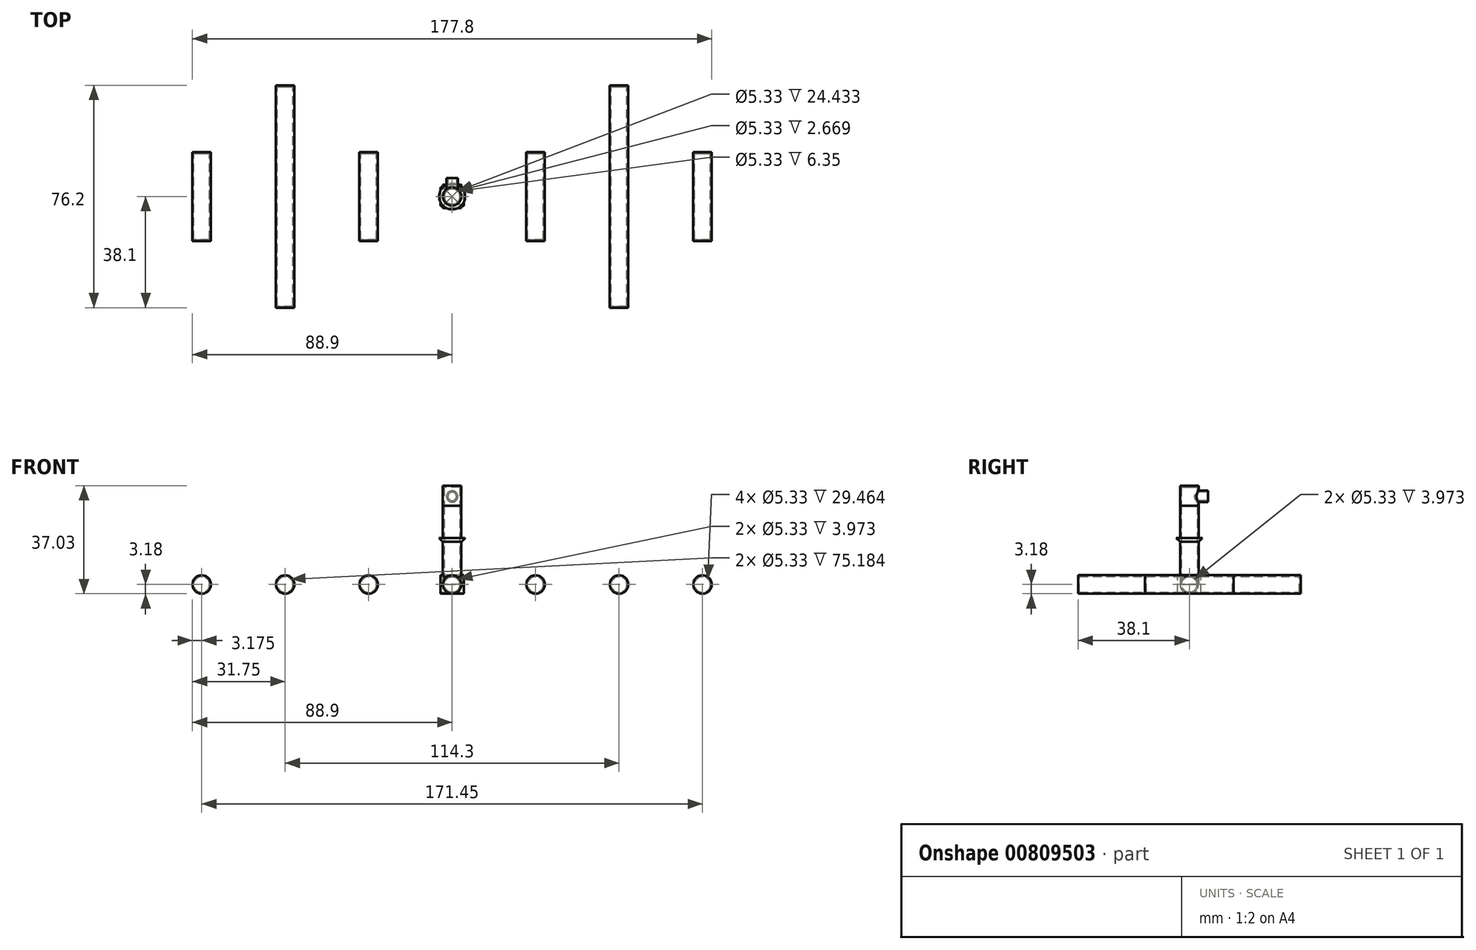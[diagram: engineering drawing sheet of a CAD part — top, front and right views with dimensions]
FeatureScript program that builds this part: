
annotation { "Feature Type Name" : "Feature", "Feature Type Description" : "" }
export const myFeature = defineFeature(function(context is Context, id is Id, definition is map)
    precondition{}
    {
        {
            var Q0;
            Q0=qCreatedBy(makeId("Front.planeOp"),FACE);
            var sketch = newSketch(context, id + "F0", { "sketchPlane" : qUnion([Q0])});
            skCircle(sketch, "E0", {"center": v(0, 0) * mm, "radius": 3.18 * mm});
            skCircle(sketch, "E1", {"center": v(0, 0) * mm, "radius": 2.67 * mm});
            skSolve(sketch);
        }
        {
            var Q0;
            Q0 = qSketchRegion(id + "F0", true);
            extrude(context, id + "F1", {"entities" : qUnion([Q0]), "depth" : (3 * sqrt(2) - 0.25) * mm, "offsetDistance" : 25.4 * mm, "hasSecondDirection" : true, "secondDirectionOppositeDirection" : true, "secondDirectionDepth" : (3 * sqrt(2) - 0.25) * mm});
        }
        {
            var Q0;
            Q0=makeQuery(id+"F0.imprint","IMPRINT",FACE,{"disambiguationData":[TD([[makeQuery(id+"F0.imprint","IMPRINT",EDGE,{"derivedFrom":sQuery(id+"F0.wireOp",EDGE,"E1")}),1.0]])]});
            var Q1;
            Q1=makeQuery(id+"F0.imprint","IMPRINT",FACE,{"disambiguationData":[TD([[makeQuery(id+"F0.imprint","IMPRINT",EDGE,{"derivedFrom":sQuery(id+"F0.wireOp",EDGE,"E0")}),1.0]])]});
            extrude(context, id + "F2", {"entities" : qUnion([Q0, Q1]), "operationType" : NewBodyOperationType.ADD, "depth" : (3 * sqrt(2) - 0.25) * mm, "offsetDistance" : 25.4 * mm, "hasSecondDirection" : true, "secondDirectionOppositeDirection" : false, "secondDirectionDepth" : ((3 * sqrt(2) - 0.25) - 0.02) * mm});
        }
        {
            var Q0;
            Q0=makeQuery(id+"F0.imprint","IMPRINT",FACE,{"disambiguationData":[TD([[makeQuery(id+"F0.imprint","IMPRINT",EDGE,{"derivedFrom":sQuery(id+"F0.wireOp",EDGE,"E1")}),1.0]])]});
            var Q1;
            Q1=makeQuery(id+"F0.imprint","IMPRINT",FACE,{"disambiguationData":[TD([[makeQuery(id+"F0.imprint","IMPRINT",EDGE,{"derivedFrom":sQuery(id+"F0.wireOp",EDGE,"E0")}),1.0]])]});
            extrude(context, id + "F3", {"entities" : qUnion([Q0, Q1]), "operationType" : NewBodyOperationType.ADD, "oppositeDirection" : true, "depth" : (3 * sqrt(2) - 0.25) * mm, "offsetDistance" : 25.4 * mm, "hasSecondDirection" : true, "secondDirectionOppositeDirection" : true, "secondDirectionDepth" : ((3 * sqrt(2) - 0.25) - 0.02) * mm});
        }
        {
            var Q0;
            Q0=qCreatedBy(makeId("Right.planeOp"),FACE);
            var sketch = newSketch(context, id + "F4", { "sketchPlane" : qUnion([Q0])});
            skLineSegment(sketch, "E2", {"start": v(0, 0) * mm, "end": v(0, 50.22) * mm});
            skSolve(sketch);
        }
        {
            var Q0;
            Q0=makeQuery(id+"F1.opExtrude","SWEPT_BODY",BODY,{"disambiguationData":[OSD([sQuery(id+"F0.wireOp",EDGE,"E0"),sQuery(id+"F0.wireOp",EDGE,"E1")])]});
            var Q1;
            Q1=sQuery(id+"F4.wireOp",EDGE,"E2");
            circularPattern(context, id + "F5", {"entities" : qUnion([Q0]), "axis" : qUnion([Q1]), "angle" : 360 * degree, "instanceCount" : 4, "equalSpace" : true});
        }
        {
            var Q0;
            Q0=makeQuery(id+"F5.opPattern","COPY",BODY,{"derivedFrom":makeQuery(id+"F1.opExtrude","SWEPT_BODY",BODY,{"disambiguationData":[OSD([sQuery(id+"F0.wireOp",EDGE,"E0"),sQuery(id+"F0.wireOp",EDGE,"E1")])]}),"instanceName":"3"});
            deleteBodies(context, id + "F6", {"entities" : qUnion([Q0])});
        }
        {
            var Q0;
            Q0=makeQuery(id+"F5.opPattern","COPY",BODY,{"derivedFrom":makeQuery(id+"F1.opExtrude","SWEPT_BODY",BODY,{"disambiguationData":[OSD([sQuery(id+"F0.wireOp",EDGE,"E0"),sQuery(id+"F0.wireOp",EDGE,"E1")])]}),"instanceName":"2"});
            deleteBodies(context, id + "F7", {"entities" : qUnion([Q0])});
        }
        {
            var Q0;
            Q0=qCreatedBy(makeId("Top.planeOp"),FACE);
            var sketch = newSketch(context, id + "F8", { "sketchPlane" : qUnion([Q0])});
            skLineSegment(sketch, "E3", {"start": v(0, 0) * mm, "end": v(0, 107.76) * mm, "construction": true});
            skLineSegment(sketch, "E4", {"start": v(0, 107.76) * mm, "end": v(107.76, 0) * mm});
            skLineSegment(sketch, "E5", {"start": v(107.76, 0) * mm, "end": v(0, -107.76) * mm});
            skLineSegment(sketch, "E6", {"start": v(0, -107.76) * mm, "end": v(-107.76, 0) * mm});
            skLineSegment(sketch, "E7", {"start": v(-107.76, 0) * mm, "end": v(0, 107.76) * mm});
            skSolve(sketch);
        }
        {
            var Q0;
            Q0=qCreatedBy(makeId("Front.planeOp"),FACE);
            var sketch = newSketch(context, id + "F9", { "sketchPlane" : qUnion([Q0])});
            skLineSegment(sketch, "E8", {"start": v(0, 0) * mm, "end": v(28.58, 0) * mm, "construction": true});
            skLineSegment(sketch, "E9", {"start": v(28.58, 0) * mm, "end": v(57.15, 0) * mm, "construction": true});
            skLineSegment(sketch, "E10", {"start": v(57.15, 0) * mm, "end": v(85.73, 0) * mm, "construction": true});
            skLineSegment(sketch, "E11", {"start": v(0, 0) * mm, "end": v(-28.58, 0) * mm, "construction": true});
            skLineSegment(sketch, "E12", {"start": v(-28.58, 0) * mm, "end": v(-57.15, 0) * mm, "construction": true});
            skLineSegment(sketch, "E13", {"start": v(-57.15, 0) * mm, "end": v(-85.73, 0) * mm, "construction": true});
            skLineSegment(sketch, "E14", {"start": v(0, 0) * mm, "end": v(-101.41, 0) * mm, "construction": true});
            skLineSegment(sketch, "E15", {"start": v(0, 0) * mm, "end": v(101.41, 0) * mm, "construction": true});
            skCircle(sketch, "E16", {"center": v(-85.73, 0) * mm, "radius": 3.18 * mm});
            skCircle(sketch, "E17", {"center": v(-57.15, 0) * mm, "radius": 3.18 * mm});
            skCircle(sketch, "E18", {"center": v(-28.58, 0) * mm, "radius": 3.18 * mm});
            skCircle(sketch, "E19", {"center": v(28.58, 0) * mm, "radius": 3.18 * mm});
            skCircle(sketch, "E20", {"center": v(57.15, 0) * mm, "radius": 3.18 * mm});
            skCircle(sketch, "E21", {"center": v(85.73, 0) * mm, "radius": 3.18 * mm});
            skCircle(sketch, "E22", {"center": v(-85.73, 0) * mm, "radius": 2.67 * mm});
            skCircle(sketch, "E23", {"center": v(-57.15, 0) * mm, "radius": 2.67 * mm});
            skCircle(sketch, "E24", {"center": v(-28.58, 0) * mm, "radius": 2.67 * mm});
            skCircle(sketch, "E25", {"center": v(28.58, 0) * mm, "radius": 2.67 * mm});
            skCircle(sketch, "E26", {"center": v(57.15, 0) * mm, "radius": 2.67 * mm});
            skCircle(sketch, "E27", {"center": v(85.73, 0) * mm, "radius": 2.67 * mm});
            skSolve(sketch);
        }
        {
            var Q0;
            Q0=makeQuery(id+"F9.imprint","IMPRINT",FACE,{"disambiguationData":[TD([[makeQuery(id+"F9.imprint","IMPRINT",EDGE,{"derivedFrom":sQuery(id+"F9.wireOp",EDGE,"E22")}),1.0]])]});
            var Q1;
            Q1=makeQuery(id+"F9.imprint","IMPRINT",FACE,{"disambiguationData":[TD([[makeQuery(id+"F9.imprint","IMPRINT",EDGE,{"derivedFrom":sQuery(id+"F9.wireOp",EDGE,"E23")}),1.0]])]});
            var Q2;
            Q2=makeQuery(id+"F9.imprint","IMPRINT",FACE,{"disambiguationData":[TD([[makeQuery(id+"F9.imprint","IMPRINT",EDGE,{"derivedFrom":sQuery(id+"F9.wireOp",EDGE,"E24")}),1.0]])]});
            var Q3;
            Q3=makeQuery(id+"F9.imprint","IMPRINT",FACE,{"disambiguationData":[TD([[makeQuery(id+"F9.imprint","IMPRINT",EDGE,{"derivedFrom":sQuery(id+"F9.wireOp",EDGE,"E25")}),1.0]])]});
            var Q4;
            Q4=makeQuery(id+"F9.imprint","IMPRINT",FACE,{"disambiguationData":[TD([[makeQuery(id+"F9.imprint","IMPRINT",EDGE,{"derivedFrom":sQuery(id+"F9.wireOp",EDGE,"E26")}),1.0]])]});
            var Q5;
            Q5=makeQuery(id+"F9.imprint","IMPRINT",FACE,{"disambiguationData":[TD([[makeQuery(id+"F9.imprint","IMPRINT",EDGE,{"derivedFrom":sQuery(id+"F9.wireOp",EDGE,"E27")}),1.0]])]});
            extrude(context, id + "F10", {"entities" : qUnion([Q0, Q1, Q2, Q3, Q4, Q5]), "operationType" : NewBodyOperationType.REMOVE, "oppositeDirection" : true, "depth" : 25.4 * mm, "offsetDistance" : 25.4 * mm, "hasSecondDirection" : true, "secondDirectionOppositeDirection" : false, "secondDirectionDepth" : 25.4 * mm});
        }
        {
            var Q0;
            Q0=makeQuery(id+"F9.imprint","IMPRINT",FACE,{"disambiguationData":[TD([[makeQuery(id+"F9.imprint","IMPRINT",EDGE,{"derivedFrom":sQuery(id+"F9.wireOp",EDGE,"E16")}),1.0]])]});
            var Q1;
            Q1=makeQuery(id+"F9.imprint","IMPRINT",FACE,{"disambiguationData":[TD([[makeQuery(id+"F9.imprint","IMPRINT",EDGE,{"derivedFrom":sQuery(id+"F9.wireOp",EDGE,"E18")}),1.0]])]});
            var Q2;
            Q2=makeQuery(id+"F9.imprint","IMPRINT",FACE,{"disambiguationData":[TD([[makeQuery(id+"F9.imprint","IMPRINT",EDGE,{"derivedFrom":sQuery(id+"F9.wireOp",EDGE,"E19")}),1.0]])]});
            var Q3;
            Q3=makeQuery(id+"F9.imprint","IMPRINT",FACE,{"disambiguationData":[TD([[makeQuery(id+"F9.imprint","IMPRINT",EDGE,{"derivedFrom":sQuery(id+"F9.wireOp",EDGE,"E21")}),1.0]])]});
            extrude(context, id + "F11", {"entities" : qUnion([Q0, Q1, Q2, Q3]), "operationType" : NewBodyOperationType.ADD, "depth" : 15.24 * mm, "offsetDistance" : 25.4 * mm, "hasSecondDirection" : true, "secondDirectionOppositeDirection" : true, "secondDirectionDepth" : 15.24 * mm});
        }
        {
            var Q0;
            Q0=makeQuery(id+"F9.imprint","IMPRINT",FACE,{"disambiguationData":[TD([[makeQuery(id+"F9.imprint","IMPRINT",EDGE,{"derivedFrom":sQuery(id+"F9.wireOp",EDGE,"E22")}),1.0]])]});
            var Q1;
            Q1=makeQuery(id+"F9.imprint","IMPRINT",FACE,{"disambiguationData":[TD([[makeQuery(id+"F9.imprint","IMPRINT",EDGE,{"derivedFrom":sQuery(id+"F9.wireOp",EDGE,"E16")}),1.0]])]});
            var Q2;
            Q2=makeQuery(id+"F9.imprint","IMPRINT",FACE,{"disambiguationData":[TD([[makeQuery(id+"F9.imprint","IMPRINT",EDGE,{"derivedFrom":sQuery(id+"F9.wireOp",EDGE,"E24")}),1.0]])]});
            var Q3;
            Q3=makeQuery(id+"F9.imprint","IMPRINT",FACE,{"disambiguationData":[TD([[makeQuery(id+"F9.imprint","IMPRINT",EDGE,{"derivedFrom":sQuery(id+"F9.wireOp",EDGE,"E18")}),1.0]])]});
            var Q4;
            Q4=makeQuery(id+"F9.imprint","IMPRINT",FACE,{"disambiguationData":[TD([[makeQuery(id+"F9.imprint","IMPRINT",EDGE,{"derivedFrom":sQuery(id+"F9.wireOp",EDGE,"E25")}),1.0]])]});
            var Q5;
            Q5=makeQuery(id+"F9.imprint","IMPRINT",FACE,{"disambiguationData":[TD([[makeQuery(id+"F9.imprint","IMPRINT",EDGE,{"derivedFrom":sQuery(id+"F9.wireOp",EDGE,"E19")}),1.0]])]});
            var Q6;
            Q6=makeQuery(id+"F9.imprint","IMPRINT",FACE,{"disambiguationData":[TD([[makeQuery(id+"F9.imprint","IMPRINT",EDGE,{"derivedFrom":sQuery(id+"F9.wireOp",EDGE,"E27")}),1.0]])]});
            var Q7;
            Q7=makeQuery(id+"F9.imprint","IMPRINT",FACE,{"disambiguationData":[TD([[makeQuery(id+"F9.imprint","IMPRINT",EDGE,{"derivedFrom":sQuery(id+"F9.wireOp",EDGE,"E21")}),1.0]])]});
            extrude(context, id + "F12", {"entities" : qUnion([Q0, Q1, Q2, Q3, Q4, Q5, Q6, Q7]), "operationType" : NewBodyOperationType.ADD, "depth" : 15.24 * mm, "offsetDistance" : 25.4 * mm, "hasSecondDirection" : true, "secondDirectionOppositeDirection" : false, "secondDirectionDepth" : 14.73 * mm});
        }
        {
            var Q0;
            Q0=makeQuery(id+"F9.imprint","IMPRINT",FACE,{"disambiguationData":[TD([[makeQuery(id+"F9.imprint","IMPRINT",EDGE,{"derivedFrom":sQuery(id+"F9.wireOp",EDGE,"E22")}),1.0]])]});
            var Q1;
            Q1=makeQuery(id+"F9.imprint","IMPRINT",FACE,{"disambiguationData":[TD([[makeQuery(id+"F9.imprint","IMPRINT",EDGE,{"derivedFrom":sQuery(id+"F9.wireOp",EDGE,"E16")}),1.0]])]});
            var Q2;
            Q2=makeQuery(id+"F9.imprint","IMPRINT",FACE,{"disambiguationData":[TD([[makeQuery(id+"F9.imprint","IMPRINT",EDGE,{"derivedFrom":sQuery(id+"F9.wireOp",EDGE,"E24")}),1.0]])]});
            var Q3;
            Q3=makeQuery(id+"F9.imprint","IMPRINT",FACE,{"disambiguationData":[TD([[makeQuery(id+"F9.imprint","IMPRINT",EDGE,{"derivedFrom":sQuery(id+"F9.wireOp",EDGE,"E18")}),1.0]])]});
            var Q4;
            Q4=makeQuery(id+"F9.imprint","IMPRINT",FACE,{"disambiguationData":[TD([[makeQuery(id+"F9.imprint","IMPRINT",EDGE,{"derivedFrom":sQuery(id+"F9.wireOp",EDGE,"E25")}),1.0]])]});
            var Q5;
            Q5=makeQuery(id+"F9.imprint","IMPRINT",FACE,{"disambiguationData":[TD([[makeQuery(id+"F9.imprint","IMPRINT",EDGE,{"derivedFrom":sQuery(id+"F9.wireOp",EDGE,"E19")}),1.0]])]});
            var Q6;
            Q6=makeQuery(id+"F9.imprint","IMPRINT",FACE,{"disambiguationData":[TD([[makeQuery(id+"F9.imprint","IMPRINT",EDGE,{"derivedFrom":sQuery(id+"F9.wireOp",EDGE,"E27")}),1.0]])]});
            var Q7;
            Q7=makeQuery(id+"F9.imprint","IMPRINT",FACE,{"disambiguationData":[TD([[makeQuery(id+"F9.imprint","IMPRINT",EDGE,{"derivedFrom":sQuery(id+"F9.wireOp",EDGE,"E21")}),1.0]])]});
            extrude(context, id + "F13", {"entities" : qUnion([Q0, Q1, Q2, Q3, Q4, Q5, Q6, Q7]), "operationType" : NewBodyOperationType.ADD, "oppositeDirection" : true, "depth" : 15.24 * mm, "offsetDistance" : 25.4 * mm, "hasSecondDirection" : true, "secondDirectionOppositeDirection" : true, "secondDirectionDepth" : 14.73 * mm});
        }
        {
            var Q0;
            Q0=makeQuery(id+"F9.imprint","IMPRINT",FACE,{"disambiguationData":[TD([[makeQuery(id+"F9.imprint","IMPRINT",EDGE,{"derivedFrom":sQuery(id+"F9.wireOp",EDGE,"E17")}),1.0]])]});
            var Q1;
            Q1=makeQuery(id+"F9.imprint","IMPRINT",FACE,{"disambiguationData":[TD([[makeQuery(id+"F9.imprint","IMPRINT",EDGE,{"derivedFrom":sQuery(id+"F9.wireOp",EDGE,"E20")}),1.0]])]});
            extrude(context, id + "F14", {"entities" : qUnion([Q0, Q1]), "operationType" : NewBodyOperationType.ADD, "depth" : 38.1 * mm, "offsetDistance" : 25.4 * mm, "hasSecondDirection" : true, "secondDirectionOppositeDirection" : true, "secondDirectionDepth" : 38.1 * mm});
        }
        {
            var Q0;
            Q0=makeQuery(id+"F9.imprint","IMPRINT",FACE,{"disambiguationData":[TD([[makeQuery(id+"F9.imprint","IMPRINT",EDGE,{"derivedFrom":sQuery(id+"F9.wireOp",EDGE,"E26")}),1.0]])]});
            var Q1;
            Q1=makeQuery(id+"F9.imprint","IMPRINT",FACE,{"disambiguationData":[TD([[makeQuery(id+"F9.imprint","IMPRINT",EDGE,{"derivedFrom":sQuery(id+"F9.wireOp",EDGE,"E20")}),1.0]])]});
            var Q2;
            Q2=makeQuery(id+"F9.imprint","IMPRINT",FACE,{"disambiguationData":[TD([[makeQuery(id+"F9.imprint","IMPRINT",EDGE,{"derivedFrom":sQuery(id+"F9.wireOp",EDGE,"E23")}),1.0]])]});
            var Q3;
            Q3=makeQuery(id+"F9.imprint","IMPRINT",FACE,{"disambiguationData":[TD([[makeQuery(id+"F9.imprint","IMPRINT",EDGE,{"derivedFrom":sQuery(id+"F9.wireOp",EDGE,"E17")}),1.0]])]});
            extrude(context, id + "F15", {"entities" : qUnion([Q0, Q1, Q2, Q3]), "operationType" : NewBodyOperationType.ADD, "depth" : 38.1 * mm, "offsetDistance" : 25.4 * mm, "hasSecondDirection" : true, "secondDirectionOppositeDirection" : false, "secondDirectionDepth" : 37.6 * mm});
        }
        {
            var Q0;
            Q0=makeQuery(id+"F9.imprint","IMPRINT",FACE,{"disambiguationData":[TD([[makeQuery(id+"F9.imprint","IMPRINT",EDGE,{"derivedFrom":sQuery(id+"F9.wireOp",EDGE,"E23")}),1.0]])]});
            var Q1;
            Q1=makeQuery(id+"F9.imprint","IMPRINT",FACE,{"disambiguationData":[TD([[makeQuery(id+"F9.imprint","IMPRINT",EDGE,{"derivedFrom":sQuery(id+"F9.wireOp",EDGE,"E17")}),1.0]])]});
            var Q2;
            Q2=makeQuery(id+"F9.imprint","IMPRINT",FACE,{"disambiguationData":[TD([[makeQuery(id+"F9.imprint","IMPRINT",EDGE,{"derivedFrom":sQuery(id+"F9.wireOp",EDGE,"E26")}),1.0]])]});
            var Q3;
            Q3=makeQuery(id+"F9.imprint","IMPRINT",FACE,{"disambiguationData":[TD([[makeQuery(id+"F9.imprint","IMPRINT",EDGE,{"derivedFrom":sQuery(id+"F9.wireOp",EDGE,"E20")}),1.0]])]});
            extrude(context, id + "F16", {"entities" : qUnion([Q0, Q1, Q2, Q3]), "operationType" : NewBodyOperationType.ADD, "oppositeDirection" : true, "depth" : 38.1 * mm, "offsetDistance" : 25.4 * mm, "hasSecondDirection" : true, "secondDirectionOppositeDirection" : true, "secondDirectionDepth" : 37.6 * mm});
        }
        {
            var Q0;
            Q0=qCreatedBy(makeId("Right.planeOp"),FACE);
            var sketch = newSketch(context, id + "F17", { "sketchPlane" : qUnion([Q0])});
            skCircle(sketch, "E28", {"center": v(0, 0) * mm, "radius": 3.18 * mm});
            skCircle(sketch, "E29", {"center": v(0, 0) * mm, "radius": 2.67 * mm});
            skSolve(sketch);
        }
        {
            var Q0;
            Q0=makeQuery(id+"F17.imprint","IMPRINT",FACE,{"disambiguationData":[TD([[makeQuery(id+"F17.imprint","IMPRINT",EDGE,{"derivedFrom":sQuery(id+"F17.wireOp",EDGE,"E29")}),1.0]])]});
            extrude(context, id + "F18", {"entities" : qUnion([Q0]), "operationType" : NewBodyOperationType.REMOVE, "oppositeDirection" : true, "depth" : (3 * sqrt(2) - 0.25 - 0.02) * mm, "offsetDistance" : 25.4 * mm, "hasSecondDirection" : true, "secondDirectionOppositeDirection" : false, "secondDirectionDepth" : (3 * sqrt(2) - 0.25 - 0.02) * mm});
        }
        {
            var Q0;
            Q0=makeQuery(id+"F1.opExtrude","SWEPT_BODY",BODY,{"disambiguationData":[OSD([sQuery(id+"F0.wireOp",EDGE,"E0"),sQuery(id+"F0.wireOp",EDGE,"E1")])]});
            var Q1;
            Q1=sQuery(id+"F4.wireOp",EDGE,"E2");
            circularPattern(context, id + "F19", {"entities" : qUnion([Q0]), "axis" : qUnion([Q1]), "angle" : 360 * degree, "instanceCount" : 4, "equalSpace" : true});
        }
        {
            var Q0;
            Q0=makeQuery(id+"F19.opPattern","COPY",BODY,{"derivedFrom":makeQuery(id+"F1.opExtrude","SWEPT_BODY",BODY,{"disambiguationData":[OSD([sQuery(id+"F0.wireOp",EDGE,"E0"),sQuery(id+"F0.wireOp",EDGE,"E1")])]}),"instanceName":"3"});
            deleteBodies(context, id + "F20", {"entities" : qUnion([Q0])});
        }
        {
            var Q0;
            Q0=makeQuery(id+"F19.opPattern","COPY",BODY,{"derivedFrom":makeQuery(id+"F1.opExtrude","SWEPT_BODY",BODY,{"disambiguationData":[OSD([sQuery(id+"F0.wireOp",EDGE,"E0"),sQuery(id+"F0.wireOp",EDGE,"E1")])]}),"instanceName":"2"});
            deleteBodies(context, id + "F21", {"entities" : qUnion([Q0])});
        }
        {
            var Q0;
            Q0=qCreatedBy(makeId("Right.planeOp"),FACE);
            var sketch = newSketch(context, id + "F22", { "sketchPlane" : qUnion([Q0])});
            skCircle(sketch, "E30", {"center": v(0, 0) * mm, "radius": 3.18 * mm});
            skCircle(sketch, "E31", {"center": v(0, 0) * mm, "radius": 2.67 * mm});
            skSolve(sketch);
        }
        {
            var Q0;
            Q0=makeQuery(id+"F22.imprint","IMPRINT",FACE,{"disambiguationData":[TD([[makeQuery(id+"F22.imprint","IMPRINT",EDGE,{"derivedFrom":sQuery(id+"F22.wireOp",EDGE,"E31")}),1.0]])]});
            extrude(context, id + "F23", {"entities" : qUnion([Q0]), "operationType" : NewBodyOperationType.REMOVE, "oppositeDirection" : true, "depth" : (3 * sqrt(2) - 0.25 - 0.02) * mm, "offsetDistance" : 25.4 * mm, "hasSecondDirection" : true, "secondDirectionOppositeDirection" : false, "secondDirectionDepth" : (3 * sqrt(2) - 0.25 - 0.02) * mm});
        }
        {
            var Q0;
            Q0=qCreatedBy(makeId("Front.planeOp"),FACE);
            var sketch = newSketch(context, id + "F24", { "sketchPlane" : qUnion([Q0])});
            skCircle(sketch, "E32", {"center": v(0, 0) * mm, "radius": 3.18 * mm});
            skCircle(sketch, "E33", {"center": v(0, 0) * mm, "radius": 2.67 * mm});
            skSolve(sketch);
        }
        {
            var Q0;
            Q0=makeQuery(id+"F24.imprint","IMPRINT",FACE,{"disambiguationData":[TD([[makeQuery(id+"F24.imprint","IMPRINT",EDGE,{"derivedFrom":sQuery(id+"F24.wireOp",EDGE,"E33")}),1.0]])]});
            extrude(context, id + "F25", {"entities" : qUnion([Q0]), "operationType" : NewBodyOperationType.REMOVE, "depth" : (3 * sqrt(2) - 0.25 - 0.02) * mm, "offsetDistance" : 25.4 * mm, "hasSecondDirection" : true, "secondDirectionOppositeDirection" : true, "secondDirectionDepth" : (3 * sqrt(2) - 0.25 - 0.02) * mm});
        }
        {
            var Q0;
            Q0=qCreatedBy(makeId("Right.planeOp"),FACE);
            var sketch = newSketch(context, id + "F26", { "sketchPlane" : qUnion([Q0])});
            skLineSegment(sketch, "E34", {"start": v(0, 0) * mm, "end": v(28.58, 0) * mm, "construction": true});
            skLineSegment(sketch, "E35", {"start": v(28.58, 0) * mm, "end": v(57.15, 0) * mm, "construction": true});
            skLineSegment(sketch, "E36", {"start": v(57.15, 0) * mm, "end": v(85.73, 0) * mm, "construction": true});
            skLineSegment(sketch, "E37", {"start": v(0, 0) * mm, "end": v(-28.58, 0) * mm, "construction": true});
            skLineSegment(sketch, "E38", {"start": v(-28.58, 0) * mm, "end": v(-57.15, 0) * mm, "construction": true});
            skLineSegment(sketch, "E39", {"start": v(-57.15, 0) * mm, "end": v(-85.73, 0) * mm, "construction": true});
            skLineSegment(sketch, "E40", {"start": v(0, 0) * mm, "end": v(-101.41, 0) * mm, "construction": true});
            skLineSegment(sketch, "E41", {"start": v(0, 0) * mm, "end": v(101.41, 0) * mm, "construction": true});
            skCircle(sketch, "E42", {"center": v(-85.73, 0) * mm, "radius": 3.18 * mm});
            skCircle(sketch, "E43", {"center": v(-57.15, 0) * mm, "radius": 3.18 * mm});
            skCircle(sketch, "E44", {"center": v(-28.58, 0) * mm, "radius": 3.18 * mm});
            skCircle(sketch, "E45", {"center": v(28.58, 0) * mm, "radius": 3.18 * mm});
            skCircle(sketch, "E46", {"center": v(57.15, 0) * mm, "radius": 3.18 * mm});
            skCircle(sketch, "E47", {"center": v(85.73, 0) * mm, "radius": 3.18 * mm});
            skCircle(sketch, "E48", {"center": v(-85.73, 0) * mm, "radius": 2.67 * mm});
            skCircle(sketch, "E49", {"center": v(-57.15, 0) * mm, "radius": 2.67 * mm});
            skCircle(sketch, "E50", {"center": v(-28.58, 0) * mm, "radius": 2.67 * mm});
            skCircle(sketch, "E51", {"center": v(28.58, 0) * mm, "radius": 2.67 * mm});
            skCircle(sketch, "E52", {"center": v(57.15, 0) * mm, "radius": 2.67 * mm});
            skCircle(sketch, "E53", {"center": v(85.73, 0) * mm, "radius": 2.67 * mm});
            skSolve(sketch);
        }
        {
            var Q0;
            Q0=makeQuery(id+"F26.imprint","IMPRINT",FACE,{"disambiguationData":[TD([[makeQuery(id+"F26.imprint","IMPRINT",EDGE,{"derivedFrom":sQuery(id+"F26.wireOp",EDGE,"E48")}),1.0]])]});
            var Q1;
            Q1=makeQuery(id+"F26.imprint","IMPRINT",FACE,{"disambiguationData":[TD([[makeQuery(id+"F26.imprint","IMPRINT",EDGE,{"derivedFrom":sQuery(id+"F26.wireOp",EDGE,"E49")}),1.0]])]});
            var Q2;
            Q2=makeQuery(id+"F26.imprint","IMPRINT",FACE,{"disambiguationData":[TD([[makeQuery(id+"F26.imprint","IMPRINT",EDGE,{"derivedFrom":sQuery(id+"F26.wireOp",EDGE,"E50")}),1.0]])]});
            var Q3;
            Q3=makeQuery(id+"F26.imprint","IMPRINT",FACE,{"disambiguationData":[TD([[makeQuery(id+"F26.imprint","IMPRINT",EDGE,{"derivedFrom":sQuery(id+"F26.wireOp",EDGE,"E51")}),1.0]])]});
            var Q4;
            Q4=makeQuery(id+"F26.imprint","IMPRINT",FACE,{"disambiguationData":[TD([[makeQuery(id+"F26.imprint","IMPRINT",EDGE,{"derivedFrom":sQuery(id+"F26.wireOp",EDGE,"E52")}),1.0]])]});
            var Q5;
            Q5=makeQuery(id+"F26.imprint","IMPRINT",FACE,{"disambiguationData":[TD([[makeQuery(id+"F26.imprint","IMPRINT",EDGE,{"derivedFrom":sQuery(id+"F26.wireOp",EDGE,"E53")}),1.0]])]});
            extrude(context, id + "F27", {"entities" : qUnion([Q0, Q1, Q2, Q3, Q4, Q5]), "operationType" : NewBodyOperationType.REMOVE, "oppositeDirection" : true, "depth" : 12.7 * mm, "offsetDistance" : 25.4 * mm, "hasSecondDirection" : true, "secondDirectionOppositeDirection" : false, "secondDirectionDepth" : 12.7 * mm});
        }
        {
            var Q0;
            Q0=makeQuery(id+"F9.imprint","IMPRINT",FACE,{"disambiguationData":[TD([[makeQuery(id+"F9.imprint","IMPRINT",EDGE,{"derivedFrom":sQuery(id+"F9.wireOp",EDGE,"E22")}),1.0]])]});
            var Q1;
            Q1=makeQuery(id+"F9.imprint","IMPRINT",FACE,{"disambiguationData":[TD([[makeQuery(id+"F9.imprint","IMPRINT",EDGE,{"derivedFrom":sQuery(id+"F9.wireOp",EDGE,"E23")}),1.0]])]});
            var Q2;
            Q2=makeQuery(id+"F9.imprint","IMPRINT",FACE,{"disambiguationData":[TD([[makeQuery(id+"F9.imprint","IMPRINT",EDGE,{"derivedFrom":sQuery(id+"F9.wireOp",EDGE,"E24")}),1.0]])]});
            var Q3;
            Q3=makeQuery(id+"F9.imprint","IMPRINT",FACE,{"disambiguationData":[TD([[makeQuery(id+"F9.imprint","IMPRINT",EDGE,{"derivedFrom":sQuery(id+"F9.wireOp",EDGE,"E25")}),1.0]])]});
            var Q4;
            Q4=makeQuery(id+"F9.imprint","IMPRINT",FACE,{"disambiguationData":[TD([[makeQuery(id+"F9.imprint","IMPRINT",EDGE,{"derivedFrom":sQuery(id+"F9.wireOp",EDGE,"E26")}),1.0]])]});
            var Q5;
            Q5=makeQuery(id+"F9.imprint","IMPRINT",FACE,{"disambiguationData":[TD([[makeQuery(id+"F9.imprint","IMPRINT",EDGE,{"derivedFrom":sQuery(id+"F9.wireOp",EDGE,"E27")}),1.0]])]});
            extrude(context, id + "F28", {"entities" : qUnion([Q0, Q1, Q2, Q3, Q4, Q5]), "operationType" : NewBodyOperationType.REMOVE, "oppositeDirection" : true, "depth" : 12.7 * mm, "offsetDistance" : 25.4 * mm, "hasSecondDirection" : true, "secondDirectionOppositeDirection" : false, "secondDirectionDepth" : 12.7 * mm});
        }
        {
            var Q0;
            Q0=qCreatedBy(makeId("Top.planeOp"),FACE);
            var sketch = newSketch(context, id + "F29", { "sketchPlane" : qUnion([Q0])});
            skCircle(sketch, "E54", {"center": v(0, 0) * mm, "radius": 3.18 * mm});
            skCircle(sketch, "E55", {"center": v(0, 0) * mm, "radius": 2.67 * mm});
            skSolve(sketch);
        }
        {
            var Q0;
            Q0 = qSketchRegion(id + "F29", true);
            extrude(context, id + "F30", {"entities" : qUnion([Q0]), "operationType" : NewBodyOperationType.ADD, "depth" : 26.99 * mm, "offsetDistance" : 25.4 * mm});
        }
        {
            var Q0;
            Q0=qCreatedBy(makeId("Front.planeOp"),FACE);
            var sketch = newSketch(context, id + "F31", { "sketchPlane" : qUnion([Q0])});
            skLineSegment(sketch, "E56", {"start": v(0, 0) * mm, "end": v(0, 15.88) * mm, "construction": true});
            skLineSegment(sketch, "E57", {"start": v(0, 15.88) * mm, "end": v(-4.44, 15.88) * mm, "construction": true});
            skLineSegment(sketch, "E58", {"start": v(-3.18, 15.88) * mm, "end": v(-4.44, 15.88) * mm});
            skLineSegment(sketch, "E59", {"start": v(-4.44, 15.88) * mm, "end": v(-3.17, 14.6) * mm});
            skLineSegment(sketch, "E60", {"start": v(-3.18, 14.6) * mm, "end": v(-3.18, 15.88) * mm});
            skSolve(sketch);
        }
        {
            var Q0;
            Q0 = qSketchRegion(id + "F31", true);
            var Q1;
            Q1=sQuery(id+"F4.wireOp",EDGE,"E2");
            revolve(context, id + "F32", {"operationType" : NewBodyOperationType.ADD, "surfaceOperationType" : NewSurfaceOperationType.NEW, "entities" : qUnion([Q0]), "axis" : qUnion([Q1]), "revolveType" : RevolveType.FULL});
        }
        {
            var Q0;
            Q0=makeQuery(id+"F30.opExtrude","CAP_FACE",FACE,{"disambiguationData":[OSD([sQuery(id+"F29.wireOp",EDGE,"E54"),sQuery(id+"F29.wireOp",EDGE,"E55")])],"isStart":false});
            extrude(context, id + "F33", {"entities" : qUnion([Q0]), "depth" : 6.35 * mm, "offsetDistance" : 25.4 * mm});
        }
        {
            var Q0;
            Q0=makeQuery(id+"F33.opExtrude","CAP_FACE",FACE,{"disambiguationData":[OSD([sQuery(id+"F29.wireOp",EDGE,"E54"),sQuery(id+"F29.wireOp",EDGE,"E55")])],"isStart":false});
            var sketch = newSketch(context, id + "F34", { "sketchPlane" : qUnion([Q0])});
            skCircle(sketch, "E61", {"center": v(0, 0) * mm, "radius": 3.18 * mm});
            skSolve(sketch);
        }
        {
            var Q0;
            Q0 = qSketchRegion(id + "F34", true);
            extrude(context, id + "F35", {"entities" : qUnion([Q0]), "operationType" : NewBodyOperationType.ADD, "depth" : 0.5 * mm, "offsetDistance" : 25.4 * mm});
        }
        {
            var Q0;
            Q0=qCreatedBy(makeId("Front.planeOp"),FACE);
            var sketch = newSketch(context, id + "F36", { "sketchPlane" : qUnion([Q0])});
            skLineSegment(sketch, "E62", {"start": v(0, 0) * mm, "end": v(0, 30.16) * mm, "construction": true});
            skCircle(sketch, "E63", {"center": v(0, 30.16) * mm, "radius": 1.97 * mm});
            skCircle(sketch, "E64", {"center": v(0, 30.16) * mm, "radius": 1.46 * mm});
            skSolve(sketch);
        }
        {
            var Q0;
            Q0 = qSketchRegion(id + "F36", true);
            var Q1;
            Q1=makeQuery(id+"F36.imprint","IMPRINT",FACE,{"disambiguationData":[TD([[makeQuery(id+"F36.imprint","IMPRINT",EDGE,{"derivedFrom":sQuery(id+"F36.wireOp",EDGE,"E64")}),1.0]])]});
            extrude(context, id + "F37", {"entities" : qUnion([Q0, Q1]), "operationType" : NewBodyOperationType.REMOVE, "oppositeDirection" : true, "depth" : 25.4 * mm, "offsetDistance" : 25.4 * mm});
        }
        {
            var Q0;
            Q0=makeQuery(id+"F36.imprint","IMPRINT",FACE,{"disambiguationData":[TD([[makeQuery(id+"F36.imprint","IMPRINT",EDGE,{"derivedFrom":sQuery(id+"F36.wireOp",EDGE,"E63")}),1.0]])]});
            extrude(context, id + "F38", {"entities" : qUnion([Q0]), "oppositeDirection" : true, "depth" : 6.35 * mm, "offsetDistance" : 25.4 * mm});
        }
        {
            var Q0;
            Q0=makeQuery(id+"F34.imprint","IMPRINT",FACE,{"disambiguationData":[TD([[makeQuery(id+"F34.imprint","IMPRINT",EDGE,{"derivedFrom":makeQuery(id+"F33.opExtrude","CAP_EDGE",EDGE,{"disambiguationData":[OSD([sQuery(id+"F29.wireOp",EDGE,"E55")])],"isStart":false})}),1.0]])]});
            extrude(context, id + "F39", {"entities" : qUnion([Q0]), "operationType" : NewBodyOperationType.REMOVE, "oppositeDirection" : true, "depth" : 25.4 * mm, "offsetDistance" : 25.4 * mm});
        }
    });
